# Revit family: Legrand - Sobres de distribución XL³ S 4000 Gasolina para cables L350xh2000
name_source: partatom
category: Equipement électrique
units: mm (PartAtom-declared; Revit-internal decimal feet)

## family parameters
Basée sur le plan de construction = Non
Configuration du panneau = Deux colonnes, circuits au sein
Cote de connecteur circulaire = Utiliser le diamètre
Couper avec des vides une fois chargée = Non
Numéro OmniClass = 23.80.30.11.17
Partagée = Non
Point de calcul de pièce = Non
Titre OmniClass = Distribution Boards and Control Panels
Toujours verticalement = Oui
Type d'élément = Tableau de raccordement

## types (3) — shared parameters
Condiciones Generales de Uso = https://export.legrand.com
ETIM Class 6.0 = EC000261
Fabricant = Legrand
IK = 07
IP = 40
Materia = Acero
RAL = 9003
URL = www.legrand.fr
base 100mm = Non
base 200mm = Non
base profundidad 400mm = Non
base profundidad 400mm Altura 200mm = Non
base profundidad 600mm = Non
base profundidad 600mm Altura 200mm = Non
base profundidad 800mm = Non
base profundidad 800mm Altura 200mm = Non
kit acabado = Non
kit acabado profundidad 400mm = Non
kit acabado profundidad 600mm = Non
kit acabado profundidad 800mm = Non
panele detrás = Oui
panele lateral derecho = Oui
panele lateral izquierdo = Oui
puerta = Oui
zero-valued in all types: Elévation par défaut, hauteur socle

## per-type parameters (varying)
| type | Description | estructura 338000 | estructura 338004 | estructura 338008 | panele lateral derecho profundidad 400mm | panele lateral derecho profundidad 600mm | panele lateral derecho profundidad 800mm | panele lateral izquierdo profundidad 400mm | panele lateral izquierdo profundidad 600mm | panele lateral izquierdo profundidad 800mm | profundidad 400mm | profundidad 600mm | profundidad 800mm | puerta profundidad 400mm | puerta profundidad 600mm | puerta profundidad 800mm |
| XL³ S 4000 - Gasolina para cables - Metal - Altura 2000mm - Anchura 350mm - Profundidad 400mm | Ref 338001 + 338080 + 338061 + 338100 -XL³ S 4000 - Gasolina para cables - Metal - Altura 2000mm - Anchura 350mm - Profundidad 400mm | Oui | Non | Non | Oui | Non | Non | Oui | Non | Non | Oui | Non | Non | Oui | Non | Non |
| XL³ S 4000 - Gasolina para cables - Metal - Altura 2000mm - Anchura 350mm - Profundidad 600mm | Ref 338005 + 338080 + 338062 + 338100 - XL³ S 4000 - Gasolina para cables - Metal - Altura 2000mm - Anchura 350mm - Profundidad 600mm | Non | Oui | Non | Non | Oui | Non | Non | Oui | Non | Non | Oui | Non | Non | Oui | Non |
| XL³ S 4000 - Gasolina para cables - Metal - Altura 2000mm - Anchura 350mm - Profundidad 800mm | Ref 338009 + 338080 + 338063 + 338100 -XL³ S 4000 - Gasolina para cables - Metal - Altura 2000mm - Anchura 350mm - Profundidad 800mm | Non | Non | Oui | Non | Non | Oui | Non | Non | Oui | Non | Non | Oui | Non | Non | Oui |
